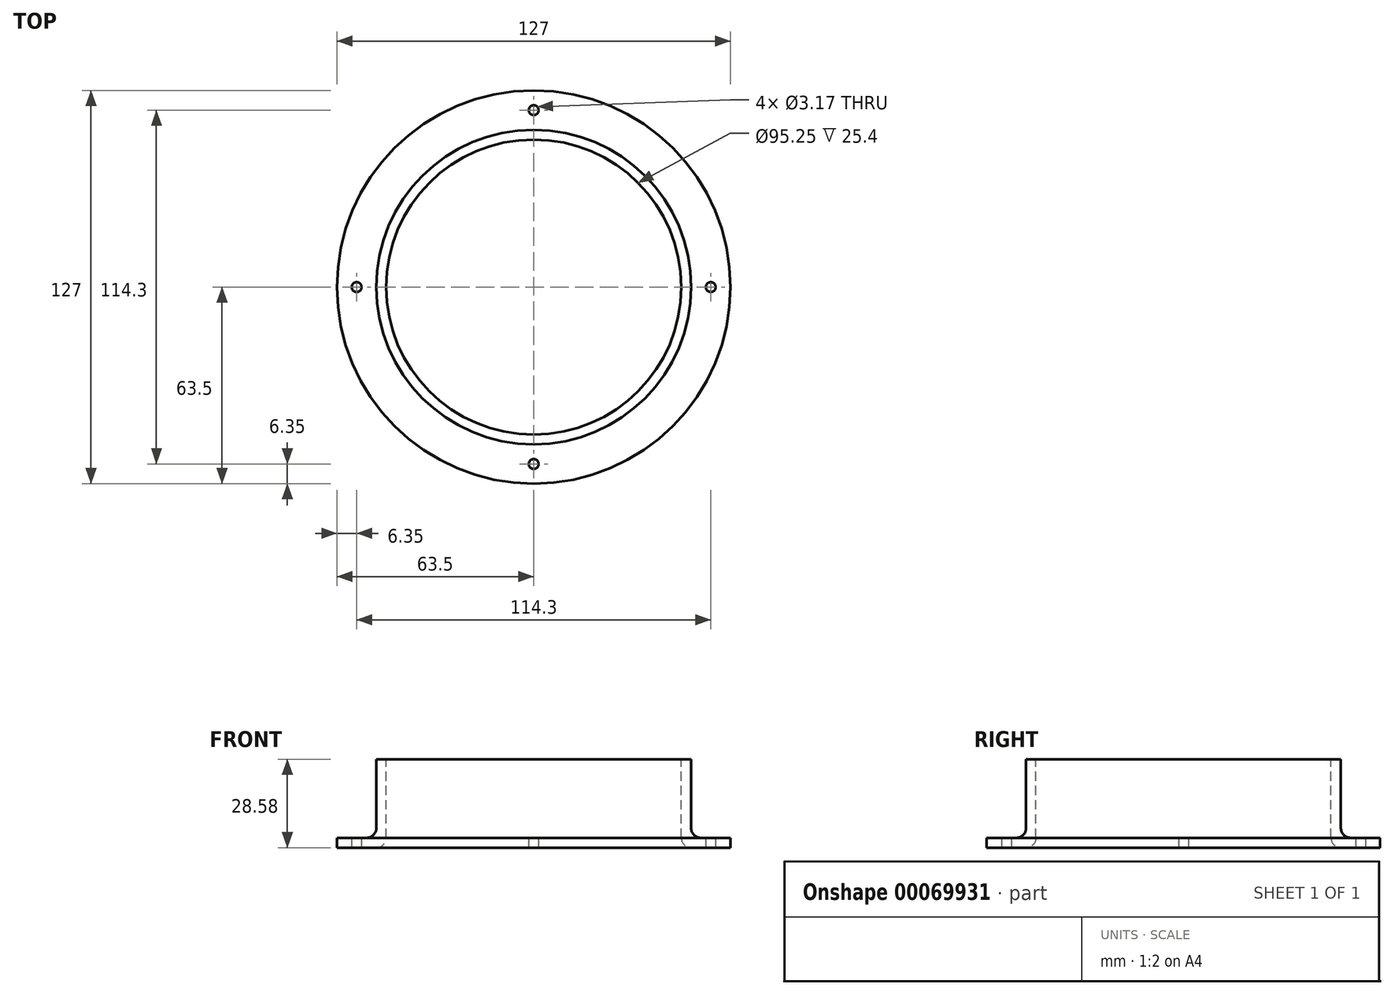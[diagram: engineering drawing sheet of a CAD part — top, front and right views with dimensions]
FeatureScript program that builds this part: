
annotation { "Feature Type Name" : "Feature", "Feature Type Description" : "" }
export const myFeature = defineFeature(function(context is Context, id is Id, definition is map)
    precondition{}
    {
        {
            var Q0;
            Q0=qCreatedBy(makeId("Front.planeOp"),FACE);
            var sketch = newSketch(context, id + "F0", { "sketchPlane" : qUnion([Q0])});
            skLineSegment(sketch, "E0", {"start": v(-63.5, 0) * mm, "end": v(-63.5, 3.18) * mm});
            skLineSegment(sketch, "E1", {"start": v(-63.5, 3.18) * mm, "end": v(-50.8, 3.18) * mm});
            skLineSegment(sketch, "E2", {"start": v(-50.8, 3.18) * mm, "end": v(-50.8, 28.58) * mm});
            skLineSegment(sketch, "E3", {"start": v(-50.8, 28.58) * mm, "end": v(-47.62, 28.58) * mm});
            skLineSegment(sketch, "E4", {"start": v(-47.62, 28.58) * mm, "end": v(-47.62, 0) * mm});
            skLineSegment(sketch, "E5", {"start": v(-63.5, 0) * mm, "end": v(-47.62, 0) * mm});
            skLineSegment(sketch, "E6", {"start": v(0, 70.27) * mm, "end": v(0, -47.64) * mm, "construction": true});
            skSolve(sketch);
        }
        {
            var Q0;
            Q0=makeQuery(id+"F0.imprint","IMPRINT",FACE,{"disambiguationData":[TD([[makeQuery(id+"F0.imprint","IMPRINT",EDGE,{"derivedFrom":sQuery(id+"F0.wireOp",EDGE,"E0")}),-1.0]])]});
            var Q1;
            Q1=sQuery(id+"F0.wireOp",EDGE,"E6");
            revolve(context, id + "F1", {"entities" : qUnion([Q0]), "axis" : qUnion([Q1]), "revolveType" : RevolveType.FULL});
        }
        {
            var Q0;
            Q0=makeQuery(id+"F1.opRevolve","SWEPT_FACE",FACE,{"disambiguationData":[OSD([sQuery(id+"F0.wireOp",EDGE,"E5")])]});
            var sketch = newSketch(context, id + "F2", { "sketchPlane" : qUnion([Q0])});
            skLineSegment(sketch, "E7", {"start": v(0, 65.55) * mm, "end": v(0, -68.08) * mm, "construction": true});
            skLineSegment(sketch, "E8", {"start": v(-68.5, 0) * mm, "end": v(68.17, 0) * mm, "construction": true});
            skPoint(sketch, "E9", {"position": v(0, -57.15) * mm});
            skPoint(sketch, "E10", {"position": v(-57.15, 0) * mm});
            skPoint(sketch, "E11", {"position": v(0, 57.15) * mm});
            skPoint(sketch, "E12", {"position": v(57.15, 0) * mm});
            skSolve(sketch);
        }
        {
            var Q0;
            Q0=sQuery(id+"F2.wireOp",VERTEX,"E10");
            var Q1;
            Q1=sQuery(id+"F2.wireOp",VERTEX,"E11");
            var Q2;
            Q2=sQuery(id+"F2.wireOp",VERTEX,"E12");
            var Q3;
            Q3=sQuery(id+"F2.wireOp",VERTEX,"E9");
            var Q4;
            Q4=makeQuery(id+"F1.opRevolve","SWEPT_BODY",BODY,{"disambiguationData":[OSD([sQuery(id+"F0.wireOp",EDGE,"E0"),sQuery(id+"F0.wireOp",EDGE,"E1"),sQuery(id+"F0.wireOp",EDGE,"E2"),sQuery(id+"F0.wireOp",EDGE,"E3"),sQuery(id+"F0.wireOp",EDGE,"E4"),sQuery(id+"F0.wireOp",EDGE,"E5")])]});
            hole(context, id + "F3", {"style" : HoleStyle.SIMPLE, "holeDiameter" : 3.17 * mm, "endStyle" : HoleEndStyle.THROUGH, "locations" : qUnion([Q0, Q1, Q2, Q3]), "scope" : qUnion([Q4])});
        }
        {
            var Q0;
            Q0=makeQuery(id+"F1.opRevolve","SWEPT_EDGE",EDGE,{"disambiguationData":[OSD([sQuery(id+"F0.wireOp",EDGE,"E4"),sQuery(id+"F0.wireOp",EDGE,"E5")])]});
            fillet(context, id + "F4", {"entities" : qUnion([Q0]), "radius" : 3.17 * mm, "tangentPropagation" : true, "allowEdgeOverflow" : false});
        }
        {
            var Q0;
            Q0=makeQuery(id+"F1.opRevolve","SWEPT_EDGE",EDGE,{"disambiguationData":[OSD([sQuery(id+"F0.wireOp",EDGE,"E1"),sQuery(id+"F0.wireOp",EDGE,"E2")])]});
            fillet(context, id + "F5", {"entities" : qUnion([Q0]), "radius" : 3.17 * mm, "tangentPropagation" : true, "allowEdgeOverflow" : false});
        }
    });
